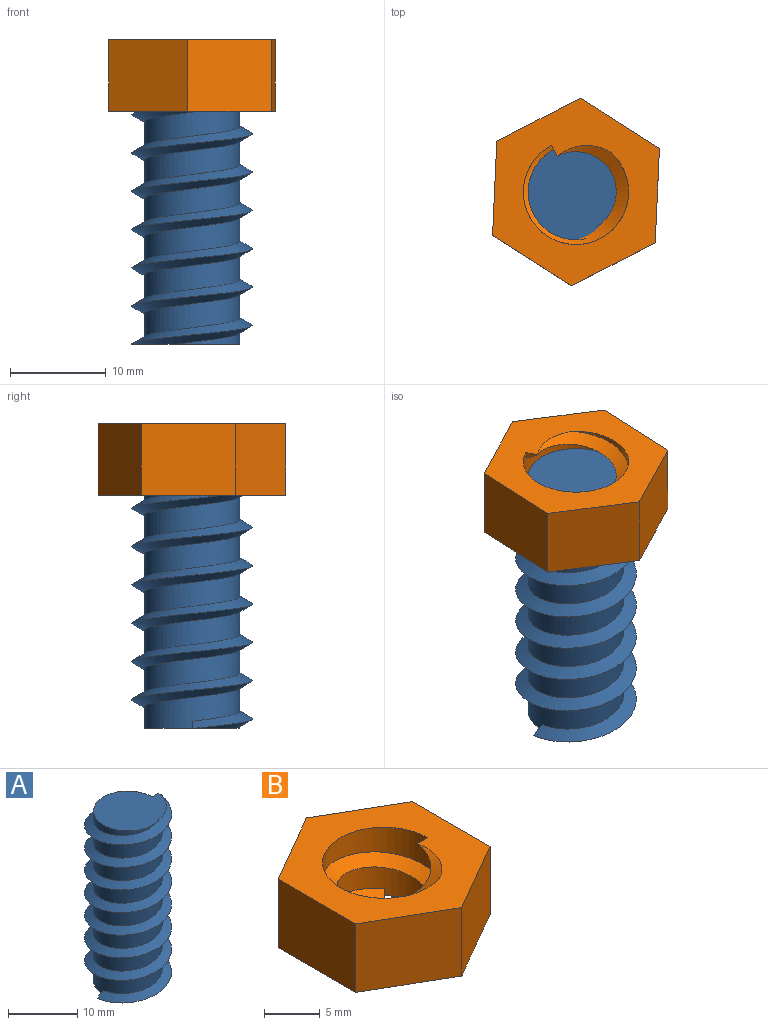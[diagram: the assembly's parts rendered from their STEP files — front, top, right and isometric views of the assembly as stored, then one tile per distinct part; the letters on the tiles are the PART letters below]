
ASSEMBLY  parts=2 mates=1
PART A: 7 faces, bbox 13x15x31.9 mm
  f0: plane 1.3x0.75mm, normal (0,1,0), area 0.5mm2, adj f2,f3,f6
  f1: bspline ~30.75x14.55mm, area 398.9mm2, adj f2,f3,f5,f6
  f2: cylinder r=5mm len=30mm, axis (0,0,-1), area 627.8mm2, adj f0,f1,f3,f4,f5,f6
  f3: plane 11.74x10.44mm, normal (0,0,1), area 82.7mm2, adj f0,f1,f2
  f4: plane 11.74x10.44mm, normal (0,0,-1), area 82.7mm2, adj f2,f5,f6
  f5: plane 1.3x0.75mm, normal (0,1,0), area 0.5mm2, adj f1,f2,f4
  f6: bspline ~30.75x14.55mm, area 398.4mm2, adj f0,f1,f2,f4
PART B: 13 faces, bbox 17.5x20.1x10 mm
  f0: plane 0.93x0.93mm, normal (0.71,-0.71,0), area 0.5mm2, adj f2,f10,f12
  f1: bspline ~12.7x11mm, area 81.9mm2, adj f2,f10,f11,f12
  f2: cylinder r=5.5mm len=11mm, axis (0,0,-1), area 167.2mm2, adj f0,f1,f9,f10,f11,f12
  f3: plane 8.5x7.5mm, normal (0.5,-0.87,0), area 73.6mm2, adj f4,f8,f9,f10
  f4: plane 9.82x7.5mm, normal (1,0,0), area 73.6mm2, adj f3,f5,f9,f10
  f5: plane 8.5x7.5mm, normal (0.5,0.87,0), area 73.6mm2, adj f4,f6,f9,f10
  f6: plane 8.5x7.5mm, normal (-0.5,0.87,0), area 73.6mm2, adj f5,f7,f9,f10
  f7: plane 9.82x7.5mm, normal (-1,0,0), area 73.6mm2, adj f6,f8,f9,f10
  f8: plane 8.5x7.5mm, normal (-0.5,-0.87,0), area 73.6mm2, adj f3,f7,f9,f10
  f9: plane 19.99x17.36mm, normal (0,0,1), area 159.1mm2, adj f2,f3,f4,f5,f6,f7,f8,f11
  f10: plane 20.1x17.47mm, normal (0,0,-1), area 159.1mm2, adj f0,f1,f2,f3,f4,f5,f6,f7
  f11: plane 1.3x0.75mm, normal (0,1,0), area 0.5mm2, adj f1,f2,f9
  f12: bspline ~12.7x11mm, area 81.8mm2, adj f0,f1,f2,f9
PLACE A t=(-21.11,-0.49,17.39)mm fixed
PLACE B rot(axis=(0,0,1),117.4deg) t=(-21.11,-0.49,41.74)mm
MATE cylindrical A.f2 <-> B.f2  axis (0,0,-1) through (-21.11,-0.49,32.39)mm
